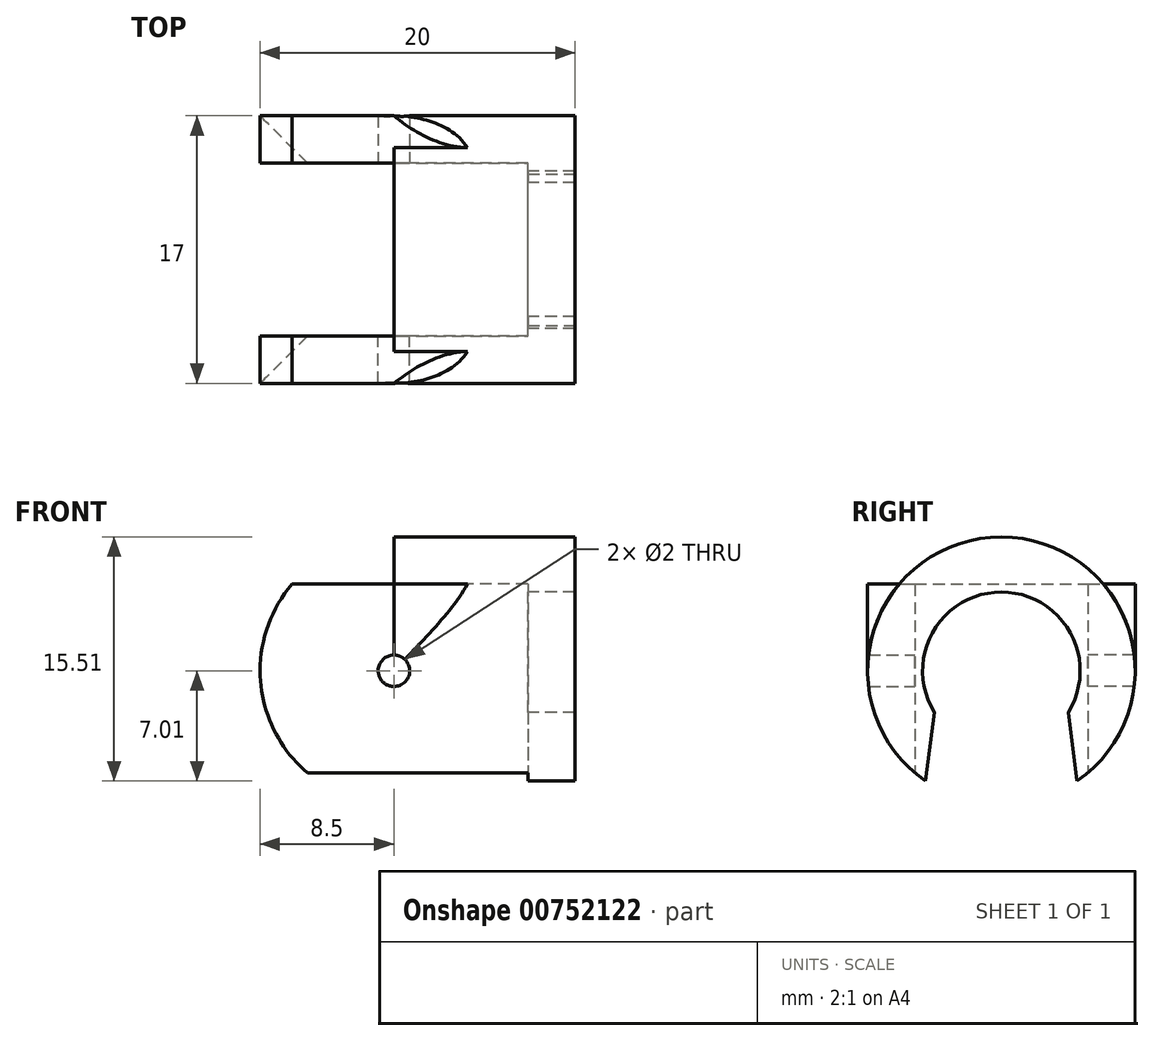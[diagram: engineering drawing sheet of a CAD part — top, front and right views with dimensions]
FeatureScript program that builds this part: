
annotation { "Feature Type Name" : "Feature", "Feature Type Description" : "" }
export const myFeature = defineFeature(function(context is Context, id is Id, definition is map)
    precondition{}
    {
        {
            var Q0;
            Q0=qCreatedBy(makeId("Front.planeOp"),FACE);
            var sketch = newSketch(context, id + "F0", { "sketchPlane" : qUnion([Q0])});
            skLineSegment(sketch, "E0.bottom", {"start": v(-38.47, 34.24) * mm, "end": v(-18.47, 34.24) * mm});
            skLineSegment(sketch, "E0.top", {"start": v(-38.47, 17.24) * mm, "end": v(-18.47, 17.24) * mm});
            skLineSegment(sketch, "E0.left", {"start": v(-38.47, 34.24) * mm, "end": v(-38.47, 17.24) * mm});
            skLineSegment(sketch, "E0.right", {"start": v(-18.47, 34.24) * mm, "end": v(-18.47, 17.24) * mm});
            skLineSegment(sketch, "E1.bottom", {"start": v(-18.47, 34.24) * mm, "end": v(-21.47, 34.24) * mm});
            skLineSegment(sketch, "E1.top", {"start": v(-18.47, 17.24) * mm, "end": v(-21.47, 17.24) * mm});
            skLineSegment(sketch, "E1.right", {"start": v(-21.47, 34.24) * mm, "end": v(-21.47, 17.24) * mm});
            skSolve(sketch);
        }
        {
            var Q0;
            Q0=makeQuery(id+"F0.imprint","IMPRINT",FACE,{"disambiguationData":[TD([[makeQuery(id+"F0.imprint","IMPRINT",EDGE,{"derivedFrom":sQuery(id+"F0.wireOp",EDGE,"E0.bottom")}),-1.0]])]});
            var Q1;
            Q1=makeQuery(id+"F0.imprint","IMPRINT",FACE,{"disambiguationData":[TD([[makeQuery(id+"F0.imprint","IMPRINT",EDGE,{"derivedFrom":sQuery(id+"F0.wireOp",EDGE,"E1.bottom")}),1.0]])]});
            extrude(context, id + "F1", {"entities" : qUnion([Q0, Q1]), "depth" : 3 * mm, "offsetDistance" : 25 * mm});
        }
        {
            var Q0;
            Q0=makeQuery(id+"F1.opExtrude","CAP_FACE",FACE,{"disambiguationData":[OSD([sQuery(id+"F0.wireOp",EDGE,"E0.bottom"),sQuery(id+"F0.wireOp",EDGE,"E0.top"),sQuery(id+"F0.wireOp",EDGE,"E0.left"),sQuery(id+"F0.wireOp",EDGE,"E1.bottom"),sQuery(id+"F0.wireOp",EDGE,"E1.top"),sQuery(id+"F0.wireOp",EDGE,"E0.right")])],"isStart":false});
            var sketch = newSketch(context, id + "F2", { "sketchPlane" : qUnion([Q0])});
            skLineSegment(sketch, "E2.bottom", {"start": v(-18.47, 34.24) * mm, "end": v(-21.47, 34.24) * mm});
            skLineSegment(sketch, "E2.top", {"start": v(-18.47, 17.24) * mm, "end": v(-21.47, 17.24) * mm});
            skLineSegment(sketch, "E2.left", {"start": v(-18.47, 34.24) * mm, "end": v(-18.47, 17.24) * mm});
            skLineSegment(sketch, "E2.right", {"start": v(-21.47, 34.24) * mm, "end": v(-21.47, 17.24) * mm});
            skLineSegment(sketch, "E3.bottom", {"start": v(-18.47, 34.24) * mm, "end": v(-38.47, 34.24) * mm});
            skLineSegment(sketch, "E3.top", {"start": v(-18.47, 31.24) * mm, "end": v(-38.47, 31.24) * mm});
            skLineSegment(sketch, "E3.left", {"start": v(-18.47, 34.24) * mm, "end": v(-18.47, 31.24) * mm});
            skLineSegment(sketch, "E3.right", {"start": v(-38.47, 34.24) * mm, "end": v(-38.47, 31.24) * mm});
            skSolve(sketch);
        }
        {
            var Q0;
            Q0=makeQuery(id+"F2.imprint","IMPRINT",FACE,{"disambiguationData":[TD([[makeQuery(id+"F2.imprint","IMPRINT",EDGE,{"derivedFrom":sQuery(id+"F2.wireOp",EDGE,"E2.bottom")}),-1.0]])]});
            var Q1;
            {var subQ0=sQuery(id+"F2.wireOp",EDGE,"E2.top");Q1=makeQuery(id+"F2.imprint","IMPRINT",FACE,{"disambiguationData":[TD([[makeQuery(id+"F2.imprint","IMPRINT",EDGE,{"derivedFrom":subQ0}),1.0]])]});}
            var Q2;
            {var subQ5=sQuery(id+"F2.wireOp",EDGE,"E3.left");Q2=makeQuery(id+"F2.imprint","IMPRINT",FACE,{"disambiguationData":[TD([[makeQuery(id+"F2.imprint","IMPRINT",EDGE,{"derivedFrom":subQ5}),-1.0]])]});}
            var Q3;
            {var subQ5=sQuery(id+"F2.wireOp",EDGE,"E3.right");Q3=makeQuery(id+"F2.imprint","IMPRINT",FACE,{"disambiguationData":[TD([[makeQuery(id+"F2.imprint","IMPRINT",EDGE,{"derivedFrom":subQ5}),1.0]])]});}
            extrude(context, id + "F3", {"entities" : qUnion([Q0, Q1, Q2, Q3]), "operationType" : NewBodyOperationType.ADD, "depth" : (11 / 2) * mm, "offsetDistance" : 25 * mm});
        }
        {
            var Q0;
            Q0=makeQuery(id+"F3.opExtrude","SWEPT_FACE",FACE,{"disambiguationData":[OSD([sQuery(id+"F2.wireOp",EDGE,"E2.right")])]});
            var sketch = newSketch(context, id + "F4", { "sketchPlane" : qUnion([Q0])});
            skCircle(sketch, "E4", {"center": v(8.5, 25.74) * mm, "radius": 5 * mm});
            skSolve(sketch);
        }
        {
            var Q0;
            {var subQ0=sQuery(id+"F4.wireOp",EDGE,"E4");var subQ1=makeQuery(id+"F3.opExtrude","CAP_EDGE",EDGE,{"disambiguationData":[OSD([sQuery(id+"F2.wireOp",EDGE,"E2.right")])],"isStart":false});var subQ2=makeQuery(id+"F4.imprint","INTERSECT",VERTEX,{"disambiguationData":[OD(0.0)],"derivedFrom":[subQ1,subQ0]});Q0=makeQuery(id+"F4.imprint","IMPRINT",FACE,{"disambiguationData":[TD([[makeQuery(id+"F4.imprint","IMPRINT",EDGE,{"disambiguationData":[TD([[subQ2,1.0]])],"derivedFrom":subQ0}),1.0]])]});}
            extrude(context, id + "F5", {"entities" : qUnion([Q0]), "operationType" : NewBodyOperationType.REMOVE, "oppositeDirection" : true, "depth" : 25 * mm, "offsetDistance" : 25 * mm});
        }
        {
            var Q0;
            Q0=makeQuery(id+"F1.opExtrude","CAP_FACE",FACE,{"disambiguationData":[OSD([sQuery(id+"F0.wireOp",EDGE,"E0.bottom"),sQuery(id+"F0.wireOp",EDGE,"E0.top"),sQuery(id+"F0.wireOp",EDGE,"E0.left"),sQuery(id+"F0.wireOp",EDGE,"E1.bottom"),sQuery(id+"F0.wireOp",EDGE,"E1.top"),sQuery(id+"F0.wireOp",EDGE,"E0.right")])],"isStart":false});
            var sketch = newSketch(context, id + "F6", { "sketchPlane" : qUnion([Q0])});
            skCircle(sketch, "E5", {"center": v(-29.97, 25.74) * mm, "radius": 5 * mm});
            skCircle(sketch, "E6", {"center": v(-29.97, 25.74) * mm, "radius": 5.5 * mm});
            skLineSegment(sketch, "E7.bottom", {"start": v(-21.47, 31.24) * mm, "end": v(-24.47, 31.24) * mm});
            skLineSegment(sketch, "E7.top", {"start": v(-21.47, 20.24) * mm, "end": v(-24.47, 20.24) * mm});
            skLineSegment(sketch, "E7.left", {"start": v(-21.47, 31.24) * mm, "end": v(-21.47, 20.24) * mm});
            skLineSegment(sketch, "E7.right", {"start": v(-24.47, 31.24) * mm, "end": v(-24.47, 20.24) * mm});
            skCircle(sketch, "E8", {"center": v(-29.97, 25.74) * mm, "radius": 1 * mm});
            skSolve(sketch);
        }
        {
            var Q0;
            Q0=makeQuery(id+"F6.imprint","IMPRINT",FACE,{"disambiguationData":[TD([[makeQuery(id+"F6.imprint","IMPRINT",EDGE,{"derivedFrom":sQuery(id+"F6.wireOp",EDGE,"E8")}),1.0]])]});
            extrude(context, id + "F7", {"entities" : qUnion([Q0]), "operationType" : NewBodyOperationType.REMOVE, "oppositeDirection" : true, "depth" : 25 * mm, "offsetDistance" : 25 * mm});
        }
        {
            var Q0;
            Q0=makeQuery(id+"F1.opExtrude","SWEPT_EDGE",EDGE,{"disambiguationData":[OSD([sQuery(id+"F0.wireOp",EDGE,"E0.top"),sQuery(id+"F0.wireOp",EDGE,"E0.left")])]});
            var Q1;
            Q1=makeQuery(id+"F3.boolean.opBoolean","MERGE",EDGE,{"derivedFrom":[makeQuery(id+"F1.opExtrude","SWEPT_EDGE",EDGE,{"disambiguationData":[OSD([sQuery(id+"F0.wireOp",EDGE,"E0.bottom"),sQuery(id+"F0.wireOp",EDGE,"E0.left")])]}),makeQuery(id+"F3.opExtrude","SWEPT_EDGE",EDGE,{"disambiguationData":[OSD([sQuery(id+"F2.wireOp",EDGE,"E3.bottom"),sQuery(id+"F2.wireOp",EDGE,"E3.right")])]})]});
            fillet(context, id + "F8", {"entities" : qUnion([Q0, Q1]), "radius" : (17 / 2) * mm, "tangentPropagation" : true, "allowEdgeOverflow" : false});
        }
        {
            var Q0;
            Q0=makeQuery(id+"F1.opExtrude","SWEPT_BODY",BODY,{"disambiguationData":[OSD([sQuery(id+"F0.wireOp",EDGE,"E0.bottom"),sQuery(id+"F0.wireOp",EDGE,"E0.top"),sQuery(id+"F0.wireOp",EDGE,"E0.left"),sQuery(id+"F0.wireOp",EDGE,"E1.bottom"),sQuery(id+"F0.wireOp",EDGE,"E1.top"),sQuery(id+"F0.wireOp",EDGE,"E0.right")])]});
            var Q1;
            {var subQ0=sQuery(id+"F2.wireOp",EDGE,"E3.left");var subQ1=sQuery(id+"F2.wireOp",EDGE,"E2.left");var subQ2=sQuery(id+"F2.wireOp",EDGE,"E2.right");var subQ3=sQuery(id+"F2.wireOp",EDGE,"E3.bottom");var subQ4=sQuery(id+"F2.wireOp",EDGE,"E3.top");var subQ5=sQuery(id+"F2.wireOp",EDGE,"E3.right");Q1=makeQuery(id+"F5.boolean.opBoolean","SPLIT",FACE,{"disambiguationData":[TD([makeQuery(id+"F1.opExtrude","SWEPT_FACE",FACE,{"disambiguationData":[OSD([sQuery(id+"F0.wireOp",EDGE,"E0.left")])]})])],"derivedFrom":makeQuery(id+"F3.opExtrude","CAP_FACE",FACE,{"disambiguationData":[OSD([sQuery(id+"F2.wireOp",EDGE,"E2.top"),subQ1,subQ2,subQ3,subQ4,subQ0,subQ5])],"isStart":false})});}
            mirror(context, id + "F9", {"operationType" : NewBodyOperationType.ADD, "entities" : qUnion([Q0]), "mirrorPlane" : qUnion([Q1])});
        }
        {
            var Q0;
            {var subQ0=makeQuery(id+"F3.opExtrude","SWEPT_FACE",FACE,{"disambiguationData":[OSD([sQuery(id+"F2.wireOp",EDGE,"E2.right")])]});Q0=makeQuery(id+"F9.boolean.opBoolean","MERGE",FACE,{"derivedFrom":[subQ0,makeQuery(id+"F9.opPattern","COPY",FACE,{"derivedFrom":subQ0,"instanceName":"1"})]});}
            var sketch = newSketch(context, id + "F10", { "sketchPlane" : qUnion([Q0])});
            skLineSegment(sketch, "E9", {"start": v(8.5, 25.74) * mm, "end": v(3.5, 25.74) * mm});
            skLineSegment(sketch, "E10", {"start": v(3.5, 25.74) * mm, "end": v(13.5, 25.74) * mm});
            skLineSegment(sketch, "E11", {"start": v(13.5, 25.74) * mm, "end": v(13.5, 17.24) * mm});
            skLineSegment(sketch, "E12", {"start": v(3.5, 25.74) * mm, "end": v(3.5, 17.24) * mm});
            skLineSegment(sketch, "E13.bottom", {"start": v(4.25, 25.74) * mm, "end": v(12.75, 25.74) * mm});
            skLineSegment(sketch, "E13.top", {"start": v(4.25, 17.24) * mm, "end": v(12.75, 17.24) * mm});
            skLineSegment(sketch, "E13.left", {"start": v(4.25, 25.74) * mm, "end": v(4.25, 17.24) * mm});
            skLineSegment(sketch, "E13.right", {"start": v(12.75, 25.74) * mm, "end": v(12.75, 17.24) * mm});
            skLineSegment(sketch, "E14", {"start": v(4.25, 23.1) * mm, "end": v(3.5, 17.24) * mm});
            skLineSegment(sketch, "E15", {"start": v(12.75, 23.1) * mm, "end": v(13.5, 17.24) * mm});
            skSolve(sketch);
        }
        {
            var Q0;
            {var subQ4=sQuery(id+"F10.wireOp",EDGE,"E14");Q0=makeQuery(id+"F10.imprint","IMPRINT",FACE,{"disambiguationData":[TD([[makeQuery(id+"F10.imprint","IMPRINT",EDGE,{"derivedFrom":subQ4}),1.0]])]});}
            var Q1;
            {var subQ0=sQuery(id+"F10.wireOp",EDGE,"E13.top");Q1=makeQuery(id+"F10.imprint","IMPRINT",FACE,{"disambiguationData":[TD([[makeQuery(id+"F10.imprint","IMPRINT",EDGE,{"derivedFrom":subQ0}),-1.0]])]});}
            var Q2;
            {var subQ4=sQuery(id+"F10.wireOp",EDGE,"E15");Q2=makeQuery(id+"F10.imprint","IMPRINT",FACE,{"disambiguationData":[TD([[makeQuery(id+"F10.imprint","IMPRINT",EDGE,{"derivedFrom":subQ4}),-1.0]])]});}
            extrude(context, id + "F11", {"entities" : qUnion([Q0, Q1, Q2]), "operationType" : NewBodyOperationType.REMOVE, "oppositeDirection" : true, "depth" : 25 * mm, "offsetDistance" : 25 * mm});
        }
        {
            var Q0;
            Q0=makeQuery(id+"F11.boolean.opBoolean","COPY",EDGE,{"derivedFrom":makeQuery(id+"F11.opExtrude","SWEPT_EDGE",EDGE,{"disambiguationData":[OSD([sQuery(id+"F4.wireOp",EDGE,"E4"),sQuery(id+"F10.wireOp",EDGE,"E13.left"),sQuery(id+"F10.wireOp",EDGE,"E14")])]})});
            var Q1;
            Q1=makeQuery(id+"F11.boolean.opBoolean","COPY",EDGE,{"derivedFrom":makeQuery(id+"F11.opExtrude","SWEPT_EDGE",EDGE,{"disambiguationData":[OSD([sQuery(id+"F4.wireOp",EDGE,"E4"),sQuery(id+"F10.wireOp",EDGE,"E13.right"),sQuery(id+"F10.wireOp",EDGE,"E15")])]})});
            fillet(context, id + "F12", {"entities" : qUnion([Q0, Q1]), "radius" : .25 * mm, "tangentPropagation" : true, "allowEdgeOverflow" : false});
        }
        {
            var Q0;
            {var subQ0=makeQuery(id+"F3.boolean.opBoolean","MERGE",FACE,{"derivedFrom":[makeQuery(id+"F1.opExtrude","SWEPT_FACE",FACE,{"disambiguationData":[OSD([sQuery(id+"F0.wireOp",EDGE,"E0.bottom"),sQuery(id+"F0.wireOp",EDGE,"E1.bottom")])]}),makeQuery(id+"F3.opExtrude","SWEPT_FACE",FACE,{"disambiguationData":[OSD([sQuery(id+"F2.wireOp",EDGE,"E3.bottom")])]})]});Q0=makeQuery(id+"F9.boolean.opBoolean","MERGE",FACE,{"derivedFrom":[subQ0,makeQuery(id+"F9.opPattern","COPY",FACE,{"derivedFrom":subQ0,"instanceName":"1"})]});}
            var sketch = newSketch(context, id + "F13", { "sketchPlane" : qUnion([Q0])});
            skLineSegment(sketch, "E16.bottom", {"start": v(-29.97, 0) * mm, "end": v(-38.47, 0) * mm});
            skLineSegment(sketch, "E16.top", {"start": v(-29.97, -17) * mm, "end": v(-38.47, -17) * mm});
            skLineSegment(sketch, "E16.left", {"start": v(-29.97, 0) * mm, "end": v(-29.97, -17) * mm});
            skLineSegment(sketch, "E16.right", {"start": v(-38.47, 0) * mm, "end": v(-38.47, -17) * mm});
            skLineSegment(sketch, "E17.bottom", {"start": v(-29.97, 0) * mm, "end": v(-26.97, 0) * mm});
            skLineSegment(sketch, "E17.top", {"start": v(-29.97, -17) * mm, "end": v(-26.97, -17) * mm});
            skLineSegment(sketch, "E17.right", {"start": v(-26.97, 0) * mm, "end": v(-26.97, -17) * mm});
            skSolve(sketch);
        }
        {
            var Q0;
            Q0=makeQuery(id+"F13.imprint","IMPRINT",FACE,{"disambiguationData":[TD([[makeQuery(id+"F13.imprint","IMPRINT",EDGE,{"derivedFrom":sQuery(id+"F13.wireOp",EDGE,"E16.bottom")}),1.0]])]});
            extrude(context, id + "F14", {"entities" : qUnion([Q0]), "operationType" : NewBodyOperationType.REMOVE, "oppositeDirection" : true, "depth" : 3 * mm, "offsetDistance" : 25 * mm});
        }
        {
            var Q0;
            {var subQ0=makeQuery(id+"F3.boolean.opBoolean","MERGE",FACE,{"derivedFrom":[makeQuery(id+"F1.opExtrude","SWEPT_FACE",FACE,{"disambiguationData":[OSD([sQuery(id+"F0.wireOp",EDGE,"E0.right")])]}),makeQuery(id+"F3.opExtrude","SWEPT_FACE",FACE,{"disambiguationData":[OSD([sQuery(id+"F2.wireOp",EDGE,"E2.left"),sQuery(id+"F2.wireOp",EDGE,"E3.left")])]})]});Q0=makeQuery(id+"F9.boolean.opBoolean","MERGE",FACE,{"derivedFrom":[subQ0,makeQuery(id+"F9.opPattern","COPY",FACE,{"derivedFrom":subQ0,"instanceName":"1"})]});}
            var sketch = newSketch(context, id + "F15", { "sketchPlane" : qUnion([Q0])});
            skCircle(sketch, "E18", {"center": v(-8.5, 25.74) * mm, "radius": 8.5 * mm});
            skSolve(sketch);
        }
        {
            var Q0;
            {var subQ0=sQuery(id+"F15.wireOp",EDGE,"E18");var subQ1=sQuery(id+"F0.wireOp",EDGE,"E0.right");var subQ5=makeQuery(id+"F9.opPattern","COPY",EDGE,{"derivedFrom":makeQuery(id+"F1.opExtrude","CAP_EDGE",EDGE,{"disambiguationData":[OSD([subQ1])],"isStart":true}),"instanceName":"1"});var subQ6=makeQuery(id+"F15.imprint","INTERSECT",VERTEX,{"derivedFrom":[subQ5,subQ0]});Q0=makeQuery(id+"F15.imprint","IMPRINT",FACE,{"disambiguationData":[TD([[makeQuery(id+"F15.imprint","IMPRINT",EDGE,{"disambiguationData":[TD([[subQ6,1.0]])],"derivedFrom":subQ0}),-1.0]])]});}
            var Q1;
            {var subQ0=sQuery(id+"F15.wireOp",EDGE,"E18");var subQ1=sQuery(id+"F0.wireOp",EDGE,"E0.right");var subQ5=makeQuery(id+"F1.opExtrude","CAP_EDGE",EDGE,{"disambiguationData":[OSD([subQ1])],"isStart":true});var subQ6=makeQuery(id+"F15.imprint","INTERSECT",VERTEX,{"derivedFrom":[subQ5,subQ0]});Q1=makeQuery(id+"F15.imprint","IMPRINT",FACE,{"disambiguationData":[TD([[makeQuery(id+"F15.imprint","IMPRINT",EDGE,{"disambiguationData":[TD([[subQ6,-1.0]])],"derivedFrom":subQ0}),-1.0]])]});}
            extrude(context, id + "F16", {"entities" : qUnion([Q0, Q1]), "operationType" : NewBodyOperationType.REMOVE, "oppositeDirection" : true, "depth" : 11.5 * mm, "offsetDistance" : 25 * mm});
        }
        {
            var Q0;
            {var subQ0=sQuery(id+"F15.wireOp",EDGE,"E18");var subQ1=sQuery(id+"F0.wireOp",EDGE,"E0.right");var subQ2=makeQuery(id+"F9.opPattern","COPY",EDGE,{"derivedFrom":makeQuery(id+"F1.opExtrude","CAP_EDGE",EDGE,{"disambiguationData":[OSD([subQ1])],"isStart":true}),"instanceName":"1"});var subQ3=makeQuery(id+"F15.imprint","INTERSECT",VERTEX,{"derivedFrom":[subQ2,subQ0]});Q0=makeQuery(id+"F15.imprint","IMPRINT",FACE,{"disambiguationData":[TD([[makeQuery(id+"F15.imprint","IMPRINT",EDGE,{"disambiguationData":[TD([[subQ3,-1.0]])],"derivedFrom":subQ0}),-1.0]])]});}
            var Q1;
            {var subQ0=sQuery(id+"F15.wireOp",EDGE,"E18");var subQ1=sQuery(id+"F0.wireOp",EDGE,"E0.right");var subQ2=makeQuery(id+"F1.opExtrude","CAP_EDGE",EDGE,{"disambiguationData":[OSD([subQ1])],"isStart":true});var subQ3=makeQuery(id+"F15.imprint","INTERSECT",VERTEX,{"derivedFrom":[subQ2,subQ0]});Q1=makeQuery(id+"F15.imprint","IMPRINT",FACE,{"disambiguationData":[TD([[makeQuery(id+"F15.imprint","IMPRINT",EDGE,{"disambiguationData":[TD([[subQ3,1.0]])],"derivedFrom":subQ0}),-1.0]])]});}
            extrude(context, id + "F17", {"entities" : qUnion([Q0, Q1]), "operationType" : NewBodyOperationType.REMOVE, "oppositeDirection" : true, "depth" : 25 * mm, "offsetDistance" : 25 * mm});
        }
        {
            var Q0;
            {var subQ0=sQuery(id+"F15.wireOp",EDGE,"E18");var subQ1=sQuery(id+"F0.wireOp",EDGE,"E0.right");Q0=makeQuery(id+"F16.boolean.opBoolean","COPY",EDGE,{"derivedFrom":makeQuery(id+"F16.opExtrude","CAP_EDGE",EDGE,{"disambiguationData":[OSD([subQ0]),TDD([makeQuery(id+"F15.imprint","IMPRINT",EDGE,{"disambiguationData":[TD([[makeQuery(id+"F15.imprint","INTERSECT",VERTEX,{"derivedFrom":[makeQuery(id+"F9.opPattern","COPY",EDGE,{"derivedFrom":makeQuery(id+"F1.opExtrude","CAP_EDGE",EDGE,{"disambiguationData":[OSD([subQ1])],"isStart":true}),"instanceName":"1"}),subQ0]}),1.0]])],"derivedFrom":subQ0})])],"isStart":false})});}
            var Q1;
            {var subQ0=sQuery(id+"F15.wireOp",EDGE,"E18");var subQ1=sQuery(id+"F0.wireOp",EDGE,"E0.right");Q1=makeQuery(id+"F16.boolean.opBoolean","COPY",EDGE,{"derivedFrom":makeQuery(id+"F16.opExtrude","CAP_EDGE",EDGE,{"disambiguationData":[OSD([subQ0]),TDD([makeQuery(id+"F15.imprint","IMPRINT",EDGE,{"disambiguationData":[TD([[makeQuery(id+"F15.imprint","INTERSECT",VERTEX,{"derivedFrom":[makeQuery(id+"F1.opExtrude","CAP_EDGE",EDGE,{"disambiguationData":[OSD([subQ1])],"isStart":true}),subQ0]}),-1.0]])],"derivedFrom":subQ0})])],"isStart":false})});}
            fillet(context, id + "F18", {"entities" : qUnion([Q0, Q1]), "radius" : 5 * mm, "tangentPropagation" : true, "allowEdgeOverflow" : false});
        }
    });
